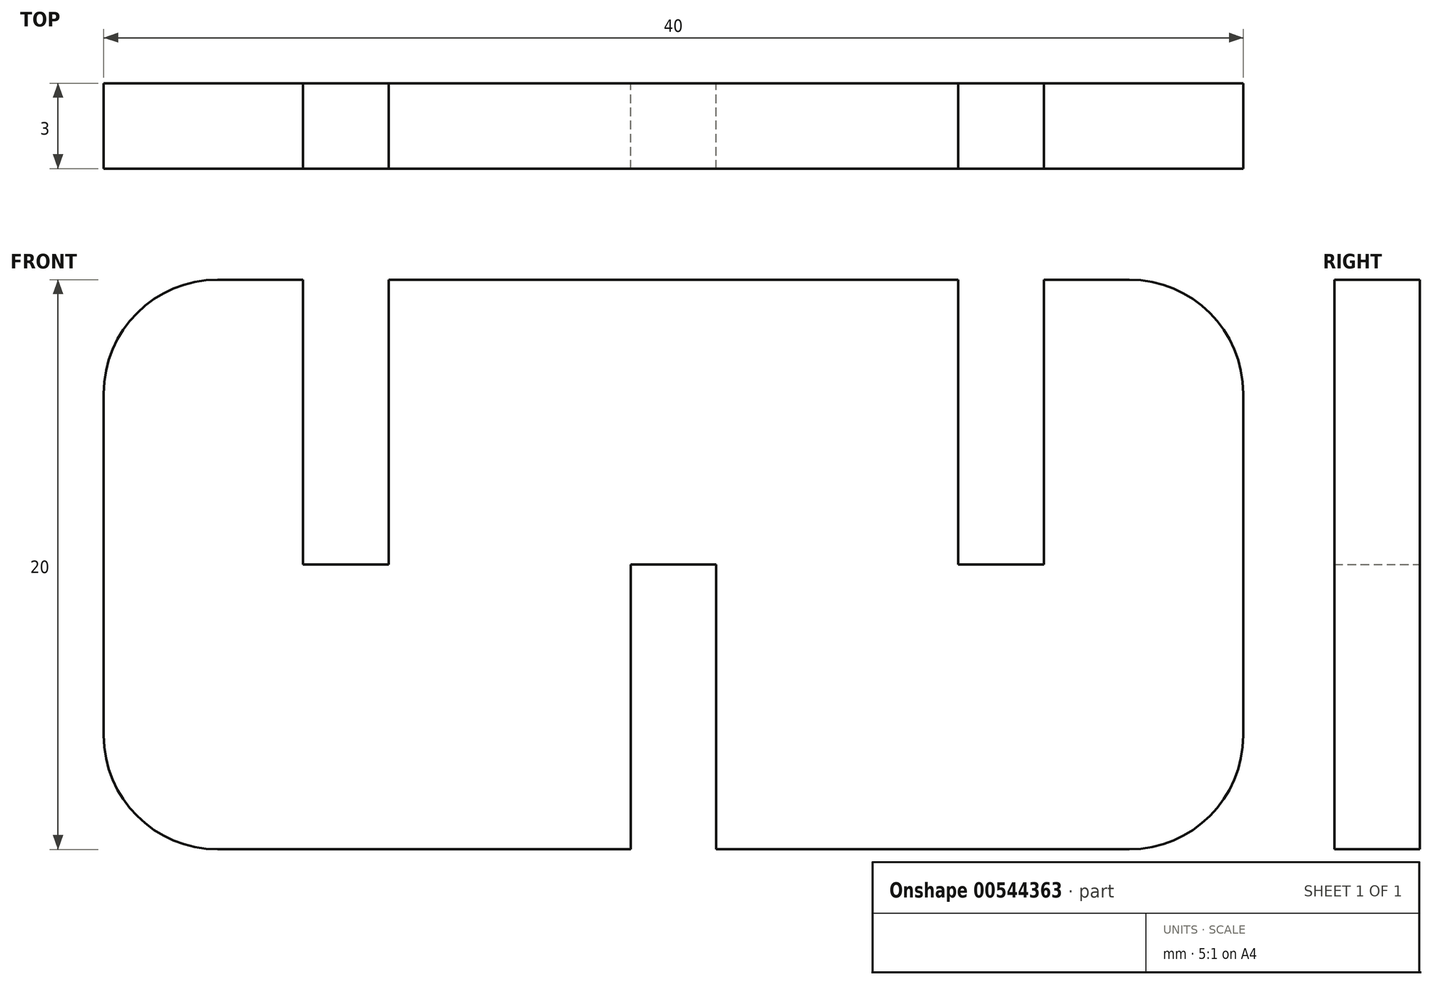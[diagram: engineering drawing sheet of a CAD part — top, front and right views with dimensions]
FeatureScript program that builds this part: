
annotation { "Feature Type Name" : "Feature", "Feature Type Description" : "" }
export const myFeature = defineFeature(function(context is Context, id is Id, definition is map)
    precondition{}
    {
        {
            var Q0;
            Q0=qCreatedBy(makeId("Front.planeOp"),FACE);
            var sketch = newSketch(context, id + "F0", { "sketchPlane" : qUnion([Q0])});
            skLineSegment(sketch, "E0", {"start": v(-17.5, 31.3) * mm, "end": v(-14.5, 31.3) * mm});
            skLineSegment(sketch, "E1", {"start": v(-21.5, 27.3) * mm, "end": v(-21.5, 15.3) * mm});
            skLineSegment(sketch, "E2", {"start": v(-17.5, 11.3) * mm, "end": v(-3, 11.3) * mm});
            skLineSegment(sketch, "E3", {"start": v(18.5, 15.3) * mm, "end": v(18.5, 27.3) * mm});
            skLineSegment(sketch, "E4", {"start": v(-14.5, 31.3) * mm, "end": v(-14.5, 21.3) * mm});
            skLineSegment(sketch, "E5", {"start": v(-14.5, 21.3) * mm, "end": v(-11.5, 21.3) * mm});
            skLineSegment(sketch, "E6", {"start": v(-11.5, 21.3) * mm, "end": v(-11.5, 31.3) * mm});
            skLineSegment(sketch, "E7.trimOffspring", {"start": v(-11.5, 31.3) * mm, "end": v(8.5, 31.3) * mm});
            skLineSegment(sketch, "E8", {"start": v(11.5, 31.3) * mm, "end": v(11.5, 21.3) * mm});
            skLineSegment(sketch, "E9", {"start": v(11.5, 21.3) * mm, "end": v(8.5, 21.3) * mm});
            skLineSegment(sketch, "E10", {"start": v(8.5, 21.3) * mm, "end": v(8.5, 31.3) * mm});
            skLineSegment(sketch, "E11.trimOffspring", {"start": v(11.5, 31.3) * mm, "end": v(14.5, 31.3) * mm});
            skLineSegment(sketch, "E12", {"start": v(-3, 11.3) * mm, "end": v(-3, 21.3) * mm});
            skLineSegment(sketch, "E13", {"start": v(-3, 21.3) * mm, "end": v(0, 21.3) * mm});
            skLineSegment(sketch, "E14", {"start": v(0, 21.3) * mm, "end": v(0, 11.3) * mm});
            skLineSegment(sketch, "E15.trimOffspring", {"start": v(0, 11.3) * mm, "end": v(14.5, 11.3) * mm});
            skPoint(sketch, "E16.visualSharp", {"position": v(-21.5, 31.3) * mm});
            skArc(sketch, "E16.filletArc", {"start": v(-17.5, 31.3) * mm, "mid": v(-20.33, 30.13) * mm, "end": v(-21.5, 27.3) * mm});
            skPoint(sketch, "E17.visualSharp", {"position": v(18.5, 31.3) * mm});
            skArc(sketch, "E17.filletArc", {"start": v(18.5, 27.3) * mm, "mid": v(17.33, 30.13) * mm, "end": v(14.5, 31.3) * mm});
            skPoint(sketch, "E18.visualSharp", {"position": v(18.5, 11.3) * mm});
            skArc(sketch, "E18.filletArc", {"start": v(14.5, 11.3) * mm, "mid": v(17.33, 12.47) * mm, "end": v(18.5, 15.3) * mm});
            skPoint(sketch, "E19.visualSharp", {"position": v(-21.5, 11.3) * mm});
            skArc(sketch, "E19.filletArc", {"start": v(-21.5, 15.3) * mm, "mid": v(-20.33, 12.47) * mm, "end": v(-17.5, 11.3) * mm});
            skSolve(sketch);
        }
        {
            var Q0;
            Q0=makeQuery(id+"F0.imprint","IMPRINT",FACE,{"disambiguationData":[TD([[makeQuery(id+"F0.imprint","IMPRINT",EDGE,{"derivedFrom":sQuery(id+"F0.wireOp",EDGE,"E0")}),-1.0]])]});
            extrude(context, id + "F1", {"entities" : qUnion([Q0]), "depth" : 3 * mm, "offsetDistance" : 25 * mm});
        }
    });
